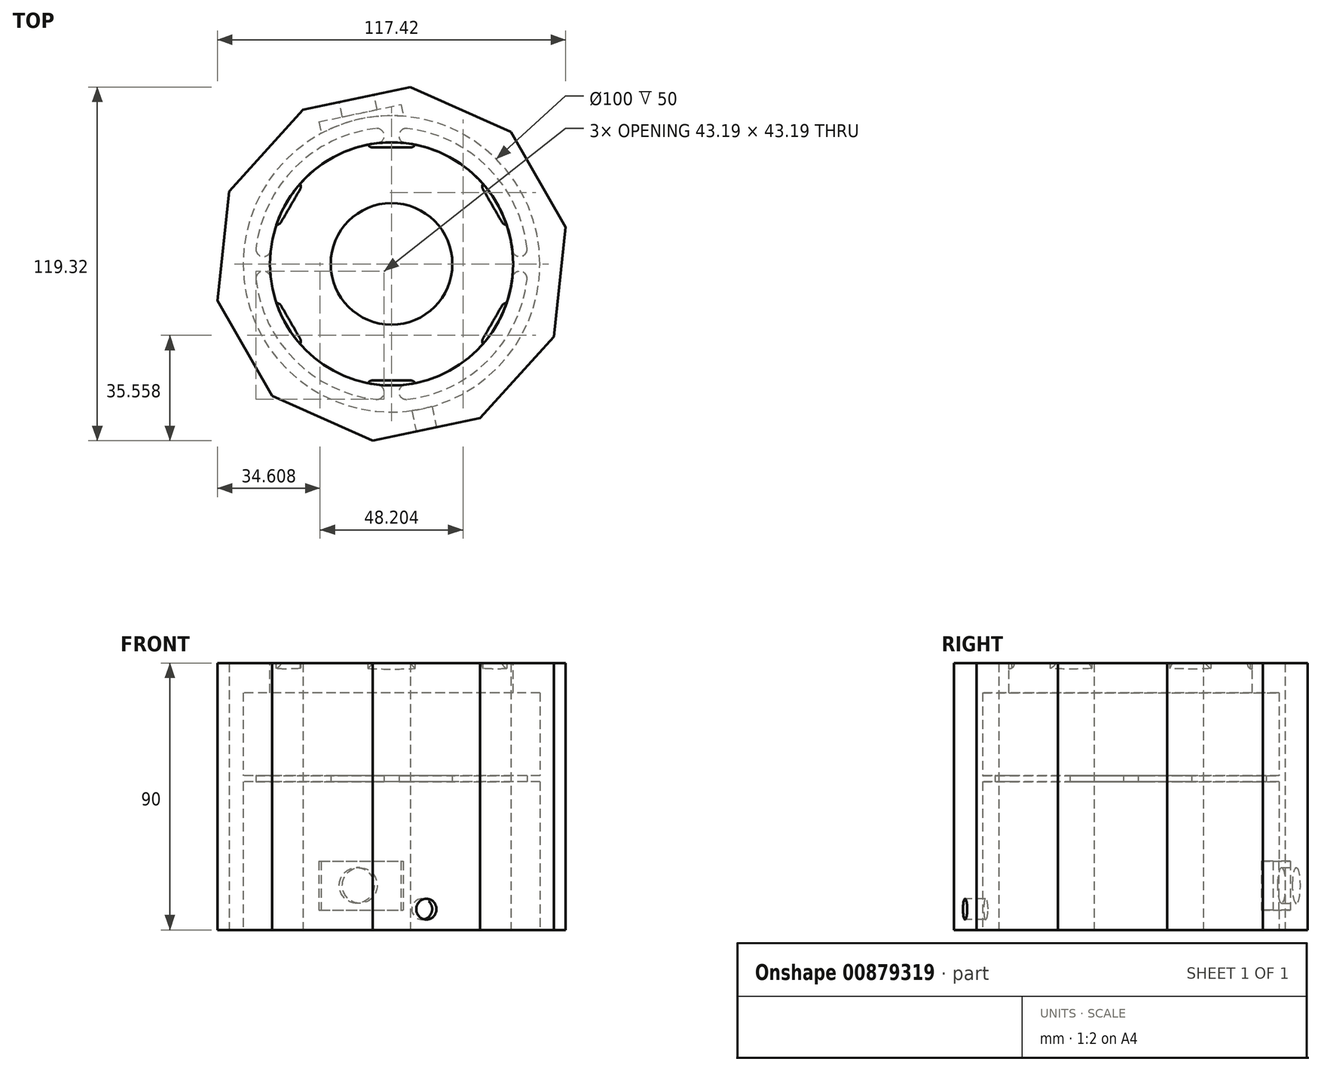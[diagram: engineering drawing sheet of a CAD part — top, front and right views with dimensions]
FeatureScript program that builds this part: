
annotation { "Feature Type Name" : "Feature", "Feature Type Description" : "" }
export const myFeature = defineFeature(function(context is Context, id is Id, definition is map)
    precondition{}
    {
        {
            var Q0;
            Q0=qCreatedBy(makeId("Top.planeOp"),FACE);
            var sketch = newSketch(context, id + "F0", { "sketchPlane" : qUnion([Q0])});
            skCircle(sketch, "E0.cCircle", {"center": v(0, 0) * mm, "radius": 60 * mm, "construction": true});
            skLineSegment(sketch, "E0.0", {"start": v(-29.9, 52.02) * mm, "end": v(6.4, 59.66) * mm});
            skLineSegment(sketch, "E0.1", {"start": v(6.4, 59.66) * mm, "end": v(40.24, 44.5) * mm});
            skLineSegment(sketch, "E0.2", {"start": v(40.24, 44.5) * mm, "end": v(58.71, 12.36) * mm});
            skLineSegment(sketch, "E0.3", {"start": v(58.71, 12.36) * mm, "end": v(54.76, -24.52) * mm});
            skLineSegment(sketch, "E0.4", {"start": v(54.76, -24.52) * mm, "end": v(29.9, -52.02) * mm});
            skLineSegment(sketch, "E0.5", {"start": v(29.9, -52.02) * mm, "end": v(-6.4, -59.66) * mm});
            skLineSegment(sketch, "E0.6", {"start": v(-6.4, -59.66) * mm, "end": v(-40.24, -44.5) * mm});
            skLineSegment(sketch, "E0.7", {"start": v(-40.24, -44.5) * mm, "end": v(-58.71, -12.36) * mm});
            skLineSegment(sketch, "E0.8", {"start": v(-58.71, -12.36) * mm, "end": v(-54.76, 24.52) * mm});
            skLineSegment(sketch, "E0.9", {"start": v(-54.76, 24.52) * mm, "end": v(-29.9, 52.02) * mm});
            skCircle(sketch, "E1", {"center": v(0, 0) * mm, "radius": 50 * mm});
            skSolve(sketch);
        }
        {
            var Q0;
            Q0=qCreatedBy(makeId("Top.planeOp"),FACE);
            cPlane(context, id + "F1", {"entities" : qUnion([Q0]), "cplaneType" : CPlaneType.OFFSET, "offset" : 50 * mm, "width" : 150 * mm, "height" : 150 * mm});
        }
        {
            var Q0;
            Q0=qCreatedBy(id+"F1.planeOp",FACE);
            var sketch = newSketch(context, id + "F2", { "sketchPlane" : qUnion([Q0])});
            skCircle(sketch, "E2", {"center": v(0, 0) * mm, "radius": 50 * mm});
            skCircle(sketch, "E3", {"center": v(0, 0) * mm, "radius": 20.5 * mm});
            skArc(sketch, "E4", {"start": v(-5.27, 45.7) * mm, "mid": v(-32.52, 32.53) * mm, "end": v(-45.7, 5.28) * mm});
            skArc(sketch, "E5", {"start": v(-4.7, 40.73) * mm, "mid": v(-28.99, 29) * mm, "end": v(-40.73, 4.7) * mm});
            skArc(sketch, "E6", {"start": v(-2.5, 43.5) * mm, "mid": v(-2.5, 43.36) * mm, "end": v(-2.48, 43.21) * mm});
            skArc(sketch, "E7", {"start": v(5.28, 45.7) * mm, "mid": v(2.5, 43.5) * mm, "end": v(4.7, 40.73) * mm});
            skPoint(sketch, "E7.first.point", {"position": v(2.5, 43.36) * mm});
            skPoint(sketch, "E7.second.point", {"position": v(4.7, 40.73) * mm});
            skPoint(sketch, "E7.third.point", {"position": v(5.28, 45.7) * mm});
            skArc(sketch, "E8", {"start": v(40.73, 4.7) * mm, "mid": v(43.5, 2.5) * mm, "end": v(45.7, 5.28) * mm});
            skPoint(sketch, "E8.first.point", {"position": v(43.36, 2.5) * mm});
            skPoint(sketch, "E8.second.point", {"position": v(40.73, 4.7) * mm});
            skPoint(sketch, "E8.third.point", {"position": v(45.7, 5.28) * mm});
            skArc(sketch, "E9", {"start": v(45.7, -5.28) * mm, "mid": v(43.5, -2.5) * mm, "end": v(40.73, -4.7) * mm});
            skPoint(sketch, "E9.first.point", {"position": v(43.36, -2.5) * mm});
            skPoint(sketch, "E9.second.point", {"position": v(40.73, -4.7) * mm});
            skPoint(sketch, "E9.third.point", {"position": v(45.7, -5.28) * mm});
            skArc(sketch, "E10", {"start": v(4.7, -40.73) * mm, "mid": v(2.5, -43.5) * mm, "end": v(5.28, -45.7) * mm});
            skPoint(sketch, "E10.first.point", {"position": v(2.5, -43.36) * mm});
            skPoint(sketch, "E10.second.point", {"position": v(4.7, -40.73) * mm});
            skPoint(sketch, "E10.third.point", {"position": v(5.28, -45.7) * mm});
            skArc(sketch, "E11", {"start": v(-5.28, -45.7) * mm, "mid": v(-2.5, -43.5) * mm, "end": v(-4.7, -40.73) * mm});
            skPoint(sketch, "E11.first.point", {"position": v(-4.7, -40.73) * mm});
            skPoint(sketch, "E11.second.point", {"position": v(-5.28, -45.7) * mm});
            skPoint(sketch, "E11.third.point", {"position": v(-2.5, -43.36) * mm});
            skArc(sketch, "E12", {"start": v(-45.7, 5.28) * mm, "mid": v(-43.5, 2.5) * mm, "end": v(-40.73, 4.7) * mm});
            skPoint(sketch, "E12.first.point", {"position": v(-43.36, 2.5) * mm});
            skPoint(sketch, "E12.second.point", {"position": v(-45.7, 5.28) * mm});
            skPoint(sketch, "E12.third.point", {"position": v(-40.73, 4.7) * mm});
            skArc(sketch, "E13", {"start": v(-40.73, -4.7) * mm, "mid": v(-43.5, -2.5) * mm, "end": v(-45.7, -5.28) * mm});
            skPoint(sketch, "E13.first.point", {"position": v(-43.36, -2.5) * mm});
            skPoint(sketch, "E13.second.point", {"position": v(-45.7, -5.28) * mm});
            skPoint(sketch, "E13.third.point", {"position": v(-40.73, -4.7) * mm});
            skArc(sketch, "E14.trimOffspring", {"start": v(45.7, 5.28) * mm, "mid": v(32.53, 32.53) * mm, "end": v(5.28, 45.7) * mm});
            skArc(sketch, "E15.trimOffspring", {"start": v(40.73, 4.7) * mm, "mid": v(29, 29) * mm, "end": v(4.7, 40.73) * mm});
            skArc(sketch, "E16.trimOffspring", {"start": v(4.7, -40.73) * mm, "mid": v(29, -29) * mm, "end": v(40.73, -4.7) * mm});
            skArc(sketch, "E17.trimOffspring", {"start": v(5.28, -45.7) * mm, "mid": v(32.53, -32.53) * mm, "end": v(45.7, -5.28) * mm});
            skArc(sketch, "E18.trimOffspring", {"start": v(-40.73, -4.7) * mm, "mid": v(-29, -29) * mm, "end": v(-4.7, -40.73) * mm});
            skArc(sketch, "E19.trimOffspring", {"start": v(-45.7, -5.28) * mm, "mid": v(-32.53, -32.53) * mm, "end": v(-5.28, -45.7) * mm});
            skArc(sketch, "E20", {"start": v(-4.7, 40.73) * mm, "mid": v(-2.5, 43.5) * mm, "end": v(-5.27, 45.7) * mm});
            skPoint(sketch, "E20.first.point", {"position": v(-5.27, 45.7) * mm});
            skPoint(sketch, "E20.second.point", {"position": v(-2.5, 43.5) * mm});
            skPoint(sketch, "E20.third.point", {"position": v(-4.7, 40.73) * mm});
            skSolve(sketch);
        }
        {
            var Q0;
            Q0 = qSketchRegion(id + "F0", true);
            extrude(context, id + "F3", {"entities" : qUnion([Q0]), "depth" : 90 * mm, "offsetDistance" : 25 * mm});
        }
        {
            var Q0;
            Q0=makeQuery(id+"F2.imprint","IMPRINT",FACE,{"disambiguationData":[TD([[makeQuery(id+"F2.imprint","IMPRINT",EDGE,{"derivedFrom":sQuery(id+"F2.wireOp",EDGE,"E2")}),1.0]])]});
            extrude(context, id + "F4", {"entities" : qUnion([Q0]), "operationType" : NewBodyOperationType.ADD, "depth" : 2 * mm, "offsetDistance" : 25 * mm});
        }
        {
            var Q0;
            Q0=qCreatedBy(makeId("Top.planeOp"),FACE);
            cPlane(context, id + "F5", {"entities" : qUnion([Q0]), "cplaneType" : CPlaneType.OFFSET, "offset" : 90 * mm, "width" : 150 * mm, "height" : 150 * mm});
        }
        {
            var Q0;
            Q0=qCreatedBy(id+"F5.planeOp",FACE);
            var sketch = newSketch(context, id + "F6", { "sketchPlane" : qUnion([Q0])});
            skCircle(sketch, "E21", {"center": v(0, 0) * mm, "radius": 41 * mm});
            skLineSegment(sketch, "E22.top", {"start": v(30.04, 26.58) * mm, "end": v(34.04, 19.65) * mm});
            skPoint(sketch, "E22.middle", {"position": v(35.5, 20.5) * mm});
            skLineSegment(sketch, "E23", {"start": v(30.04, 26.58) * mm, "end": v(30.83, 27.04) * mm});
            skLineSegment(sketch, "E24.MirrorCS", {"start": v(38.04, 12.73) * mm, "end": v(38.83, 13.18) * mm});
            skLineSegment(sketch, "E25.MirrorCS", {"start": v(38.04, 12.73) * mm, "end": v(34.04, 19.65) * mm});
            skLineSegment(sketch, "E26.1.0", {"start": v(-8, 39.3) * mm, "end": v(-8, 40.22) * mm});
            skLineSegment(sketch, "E26.1.1", {"start": v(-8, 39.3) * mm, "end": v(0, 39.3) * mm});
            skLineSegment(sketch, "E26.1.2", {"start": v(8, 39.3) * mm, "end": v(0, 39.3) * mm});
            skLineSegment(sketch, "E26.1.3", {"start": v(8, 39.3) * mm, "end": v(8, 40.22) * mm});
            skLineSegment(sketch, "E26.2.0", {"start": v(-38.03, 12.73) * mm, "end": v(-38.82, 13.18) * mm});
            skLineSegment(sketch, "E26.2.1", {"start": v(-38.03, 12.73) * mm, "end": v(-34.03, 19.65) * mm});
            skLineSegment(sketch, "E26.2.2", {"start": v(-30.03, 26.58) * mm, "end": v(-34.03, 19.65) * mm});
            skLineSegment(sketch, "E26.2.3", {"start": v(-30.03, 26.58) * mm, "end": v(-30.82, 27.04) * mm});
            skLineSegment(sketch, "E26.3.0", {"start": v(-30.03, -26.57) * mm, "end": v(-30.82, -27.03) * mm});
            skLineSegment(sketch, "E26.3.1", {"start": v(-30.03, -26.57) * mm, "end": v(-34.03, -19.65) * mm});
            skLineSegment(sketch, "E26.3.2", {"start": v(-38.03, -12.72) * mm, "end": v(-34.03, -19.65) * mm});
            skLineSegment(sketch, "E26.3.3", {"start": v(-38.03, -12.72) * mm, "end": v(-38.82, -13.17) * mm});
            skLineSegment(sketch, "E26.4.0", {"start": v(8, -39.3) * mm, "end": v(8, -40.2) * mm});
            skLineSegment(sketch, "E26.4.1", {"start": v(8, -39.3) * mm, "end": v(0, -39.3) * mm});
            skLineSegment(sketch, "E26.4.2", {"start": v(-8, -39.3) * mm, "end": v(0, -39.3) * mm});
            skLineSegment(sketch, "E26.4.3", {"start": v(-8, -39.3) * mm, "end": v(-8, -40.2) * mm});
            skLineSegment(sketch, "E26.5.0", {"start": v(38.04, -12.72) * mm, "end": v(38.83, -13.17) * mm});
            skLineSegment(sketch, "E26.5.1", {"start": v(38.04, -12.72) * mm, "end": v(34.04, -19.65) * mm});
            skLineSegment(sketch, "E26.5.2", {"start": v(30.04, -26.57) * mm, "end": v(34.04, -19.65) * mm});
            skLineSegment(sketch, "E26.5.3", {"start": v(30.04, -26.57) * mm, "end": v(30.83, -27.03) * mm});
            skCircle(sketch, "E27", {"center": v(0, 0) * mm, "radius": 50 * mm});
            skSolve(sketch);
        }
        {
            var Q0;
            Q0=makeQuery(id+"F6.imprint","IMPRINT",FACE,{"disambiguationData":[TD([[makeQuery(id+"F6.imprint","IMPRINT",EDGE,{"derivedFrom":sQuery(id+"F6.wireOp",EDGE,"E27")}),1.0]])]});
            var Q1;
            Q1=sQuery(id+"F6.wireOp",EDGE,"E27");
            var Q2;
            Q2=sQuery(id+"F6.wireOp",EDGE,"E21");
            extrude(context, id + "F7", {"entities" : qUnion([Q0]), "operationType" : NewBodyOperationType.ADD, "surfaceEntities" : qUnion([Q1, Q2]), "oppositeDirection" : true, "depth" : 10 * mm, "offsetDistance" : 25 * mm});
        }
        {
            var Q0;
            {var subQ0=sQuery(id+"F6.wireOp",EDGE,"E26.2.0");Q0=makeQuery(id+"F6.imprint","IMPRINT",FACE,{"disambiguationData":[TD([[makeQuery(id+"F6.imprint","IMPRINT",EDGE,{"derivedFrom":subQ0}),-1.0]])]});}
            var Q1;
            {var subQ0=sQuery(id+"F6.wireOp",EDGE,"E26.3.0");Q1=makeQuery(id+"F6.imprint","IMPRINT",FACE,{"disambiguationData":[TD([[makeQuery(id+"F6.imprint","IMPRINT",EDGE,{"derivedFrom":subQ0}),-1.0]])]});}
            var Q2;
            {var subQ0=sQuery(id+"F6.wireOp",EDGE,"E26.4.0");Q2=makeQuery(id+"F6.imprint","IMPRINT",FACE,{"disambiguationData":[TD([[makeQuery(id+"F6.imprint","IMPRINT",EDGE,{"derivedFrom":subQ0}),-1.0]])]});}
            var Q3;
            {var subQ0=sQuery(id+"F6.wireOp",EDGE,"E26.5.0");Q3=makeQuery(id+"F6.imprint","IMPRINT",FACE,{"disambiguationData":[TD([[makeQuery(id+"F6.imprint","IMPRINT",EDGE,{"derivedFrom":subQ0}),-1.0]])]});}
            var Q4;
            Q4=makeQuery(id+"F6.imprint","IMPRINT",FACE,{"disambiguationData":[TD([[makeQuery(id+"F6.imprint","IMPRINT",EDGE,{"derivedFrom":sQuery(id+"F6.wireOp",EDGE,"E22.top")}),1.0]])]});
            var Q5;
            {var subQ0=sQuery(id+"F6.wireOp",EDGE,"E26.1.0");Q5=makeQuery(id+"F6.imprint","IMPRINT",FACE,{"disambiguationData":[TD([[makeQuery(id+"F6.imprint","IMPRINT",EDGE,{"derivedFrom":subQ0}),-1.0]])]});}
            extrude(context, id + "F8", {"entities" : qUnion([Q0, Q1, Q2, Q3, Q4, Q5]), "oppositeDirection" : true, "depth" : 2 * mm, "offsetDistance" : 25 * mm});
        }
        {
            var Q0;
            Q0=makeQuery(id+"F8.opExtrude","CAP_EDGE",EDGE,{"disambiguationData":[OSD([sQuery(id+"F6.wireOp",EDGE,"E26.2.1"),sQuery(id+"F6.wireOp",EDGE,"E26.2.2")])],"isStart":false});
            var Q1;
            Q1=makeQuery(id+"F8.opExtrude","SWEPT_EDGE",EDGE,{"disambiguationData":[OSD([sQuery(id+"F6.wireOp",EDGE,"E26.2.2"),sQuery(id+"F6.wireOp",EDGE,"E26.2.3")])]});
            var Q2;
            Q2=makeQuery(id+"F8.opExtrude","SWEPT_EDGE",EDGE,{"disambiguationData":[OSD([sQuery(id+"F6.wireOp",EDGE,"E26.2.0"),sQuery(id+"F6.wireOp",EDGE,"E26.2.1")])]});
            var Q3;
            Q3=makeQuery(id+"F8.opExtrude","CAP_EDGE",EDGE,{"disambiguationData":[OSD([sQuery(id+"F6.wireOp",EDGE,"E26.1.1"),sQuery(id+"F6.wireOp",EDGE,"E26.1.2")])],"isStart":false});
            var Q4;
            Q4=makeQuery(id+"F8.opExtrude","SWEPT_EDGE",EDGE,{"disambiguationData":[OSD([sQuery(id+"F6.wireOp",EDGE,"E26.1.0"),sQuery(id+"F6.wireOp",EDGE,"E26.1.1")])]});
            var Q5;
            Q5=makeQuery(id+"F8.opExtrude","SWEPT_EDGE",EDGE,{"disambiguationData":[OSD([sQuery(id+"F6.wireOp",EDGE,"E26.1.2"),sQuery(id+"F6.wireOp",EDGE,"E26.1.3")])]});
            var Q6;
            Q6=makeQuery(id+"F8.opExtrude","CAP_EDGE",EDGE,{"disambiguationData":[OSD([sQuery(id+"F6.wireOp",EDGE,"E22.top"),sQuery(id+"F6.wireOp",EDGE,"E25.MirrorCS")])],"isStart":false});
            var Q7;
            Q7=makeQuery(id+"F8.opExtrude","SWEPT_EDGE",EDGE,{"disambiguationData":[OSD([sQuery(id+"F6.wireOp",EDGE,"E22.top"),sQuery(id+"F6.wireOp",EDGE,"E23")])]});
            var Q8;
            Q8=makeQuery(id+"F8.opExtrude","SWEPT_EDGE",EDGE,{"disambiguationData":[OSD([sQuery(id+"F6.wireOp",EDGE,"E24.MirrorCS"),sQuery(id+"F6.wireOp",EDGE,"E25.MirrorCS")])]});
            var Q9;
            Q9=makeQuery(id+"F8.opExtrude","CAP_EDGE",EDGE,{"disambiguationData":[OSD([sQuery(id+"F6.wireOp",EDGE,"E26.3.1"),sQuery(id+"F6.wireOp",EDGE,"E26.3.2")])],"isStart":false});
            var Q10;
            Q10=makeQuery(id+"F8.opExtrude","SWEPT_EDGE",EDGE,{"disambiguationData":[OSD([sQuery(id+"F6.wireOp",EDGE,"E26.3.2"),sQuery(id+"F6.wireOp",EDGE,"E26.3.3")])]});
            var Q11;
            Q11=makeQuery(id+"F8.opExtrude","SWEPT_EDGE",EDGE,{"disambiguationData":[OSD([sQuery(id+"F6.wireOp",EDGE,"E26.3.0"),sQuery(id+"F6.wireOp",EDGE,"E26.3.1")])]});
            var Q12;
            Q12=makeQuery(id+"F8.opExtrude","CAP_EDGE",EDGE,{"disambiguationData":[OSD([sQuery(id+"F6.wireOp",EDGE,"E26.4.1"),sQuery(id+"F6.wireOp",EDGE,"E26.4.2")])],"isStart":false});
            var Q13;
            Q13=makeQuery(id+"F8.opExtrude","SWEPT_EDGE",EDGE,{"disambiguationData":[OSD([sQuery(id+"F6.wireOp",EDGE,"E26.4.2"),sQuery(id+"F6.wireOp",EDGE,"E26.4.3")])]});
            var Q14;
            Q14=makeQuery(id+"F8.opExtrude","SWEPT_EDGE",EDGE,{"disambiguationData":[OSD([sQuery(id+"F6.wireOp",EDGE,"E26.4.0"),sQuery(id+"F6.wireOp",EDGE,"E26.4.1")])]});
            var Q15;
            Q15=makeQuery(id+"F8.opExtrude","CAP_EDGE",EDGE,{"disambiguationData":[OSD([sQuery(id+"F6.wireOp",EDGE,"E26.5.1"),sQuery(id+"F6.wireOp",EDGE,"E26.5.2")])],"isStart":false});
            var Q16;
            Q16=makeQuery(id+"F8.opExtrude","SWEPT_EDGE",EDGE,{"disambiguationData":[OSD([sQuery(id+"F6.wireOp",EDGE,"E26.5.2"),sQuery(id+"F6.wireOp",EDGE,"E26.5.3")])]});
            var Q17;
            Q17=makeQuery(id+"F8.opExtrude","SWEPT_EDGE",EDGE,{"disambiguationData":[OSD([sQuery(id+"F6.wireOp",EDGE,"E26.5.0"),sQuery(id+"F6.wireOp",EDGE,"E26.5.1")])]});
            fillet(context, id + "F9", {"entities" : qUnion([Q0, Q1, Q2, Q3, Q4, Q5, Q6, Q7, Q8, Q9, Q10, Q11, Q12, Q13, Q14, Q15, Q16, Q17]), "radius" : 2 * mm, "tangentPropagation" : true, "rho" : 0.5, "crossSection" : FilletCrossSection.CONIC, "allowEdgeOverflow" : false});
        }
        {
            var Q0;
            Q0=makeQuery(id+"F3.opExtrude","SWEPT_FACE",FACE,{"disambiguationData":[OSD([sQuery(id+"F0.wireOp",EDGE,"E0.5")])]});
            cPlane(context, id + "F10", {"entities" : qUnion([Q0]), "cplaneType" : CPlaneType.OFFSET, "offset" : 0 * mm, "width" : 150 * mm, "height" : 150 * mm});
        }
        {
            var Q0;
            Q0=qCreatedBy(id+"F10.planeOp",FACE);
            var sketch = newSketch(context, id + "F11", { "sketchPlane" : qUnion([Q0])});
            skCircle(sketch, "E28", {"center": v(0, 7) * mm, "radius": 3.5 * mm});
            skSolve(sketch);
        }
        {
            var Q0;
            Q0=makeQuery(id+"F11.imprint","IMPRINT",FACE,{"disambiguationData":[TD([[makeQuery(id+"F11.imprint","IMPRINT",EDGE,{"derivedFrom":sQuery(id+"F11.wireOp",EDGE,"E28")}),1.0]])]});
            extrude(context, id + "F12", {"entities" : qUnion([Q0]), "operationType" : NewBodyOperationType.REMOVE, "endBound" : BoundingType.UP_TO_NEXT, "oppositeDirection" : true, "depth" : 25 * mm, "offsetDistance" : 25 * mm});
        }
        {
            var Q0;
            Q0=makeQuery(id+"F3.opExtrude","SWEPT_FACE",FACE,{"disambiguationData":[OSD([sQuery(id+"F0.wireOp",EDGE,"E0.0")])]});
            cPlane(context, id + "F13", {"entities" : qUnion([Q0]), "cplaneType" : CPlaneType.OFFSET, "offset" : 0 * mm, "width" : 150 * mm, "height" : 150 * mm});
        }
        {
            var Q0;
            Q0=qCreatedBy(id+"F13.planeOp",FACE);
            var sketch = newSketch(context, id + "F14", { "sketchPlane" : qUnion([Q0])});
            skCircle(sketch, "E29", {"center": v(0, 15) * mm, "radius": 6 * mm});
            skSolve(sketch);
        }
        {
            var Q0;
            Q0=makeQuery(id+"F14.imprint","IMPRINT",FACE,{"disambiguationData":[TD([[makeQuery(id+"F14.imprint","IMPRINT",EDGE,{"derivedFrom":sQuery(id+"F14.wireOp",EDGE,"E29")}),1.0]])]});
            extrude(context, id + "F15", {"entities" : qUnion([Q0]), "operationType" : NewBodyOperationType.REMOVE, "endBound" : BoundingType.UP_TO_NEXT, "oppositeDirection" : true, "depth" : 25 * mm, "offsetDistance" : 25 * mm});
        }
        {
            var Q0;
            Q0=qCreatedBy(id+"F13.planeOp",FACE);
            cPlane(context, id + "F16", {"entities" : qUnion([Q0]), "cplaneType" : CPlaneType.OFFSET, "offset" : 9.6 * mm, "oppositeDirection" : true, "width" : 150 * mm, "height" : 150 * mm});
        }
        {
            var Q0;
            Q0=qCreatedBy(id+"F16.planeOp",FACE);
            var sketch = newSketch(context, id + "F17", { "sketchPlane" : qUnion([Q0])});
            skLineSegment(sketch, "E30.bottom", {"start": v(14.15, 23.13) * mm, "end": v(-14.15, 23.13) * mm});
            skLineSegment(sketch, "E30.top", {"start": v(14.15, 6.63) * mm, "end": v(-14.15, 6.63) * mm});
            skLineSegment(sketch, "E30.left", {"start": v(14.15, 23.13) * mm, "end": v(14.15, 6.63) * mm});
            skLineSegment(sketch, "E30.right", {"start": v(-14.15, 23.13) * mm, "end": v(-14.15, 6.63) * mm});
            skPoint(sketch, "E30.middle", {"position": v(0, 14.88) * mm});
            skSolve(sketch);
        }
        {
            var Q0;
            Q0=makeQuery(id+"F17.imprint","IMPRINT",FACE,{"disambiguationData":[TD([[makeQuery(id+"F17.imprint","IMPRINT",EDGE,{"derivedFrom":sQuery(id+"F17.wireOp",EDGE,"E30.bottom")}),1.0]])]});
            extrude(context, id + "F18", {"entities" : qUnion([Q0]), "operationType" : NewBodyOperationType.REMOVE, "depth" : 4.5 * mm, "offsetDistance" : 25 * mm});
        }
    });
